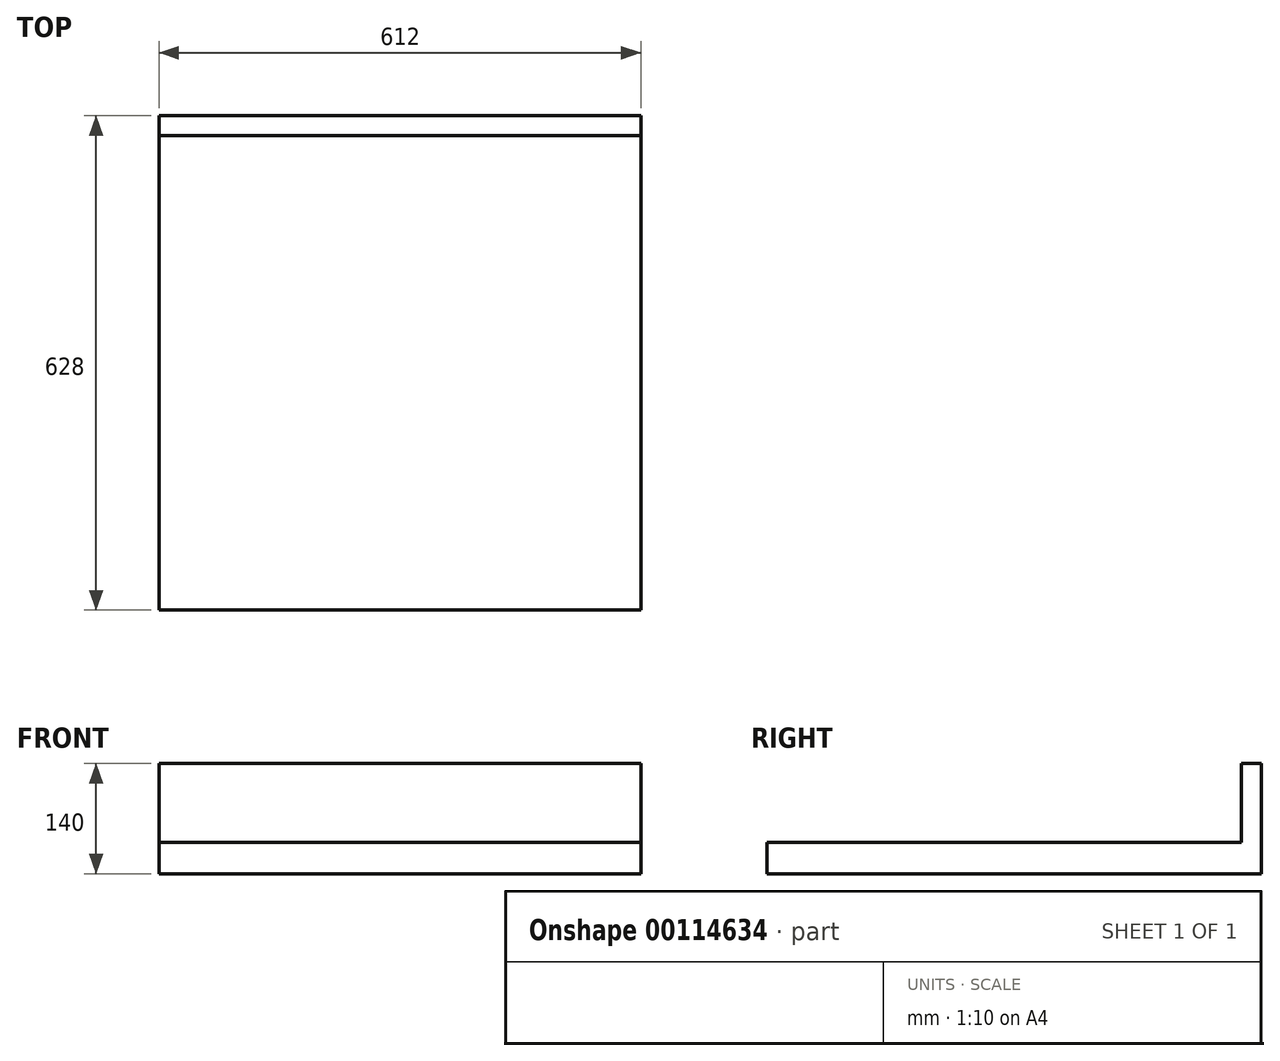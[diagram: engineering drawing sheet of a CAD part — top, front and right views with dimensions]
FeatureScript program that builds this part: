
annotation { "Feature Type Name" : "Feature", "Feature Type Description" : "" }
export const myFeature = defineFeature(function(context is Context, id is Id, definition is map)
    precondition{}
    {
        {
            var Q0;
            Q0=qCreatedBy(makeId("Front.planeOp"),FACE);
            var sketch = newSketch(context, id + "F0", { "sketchPlane" : qUnion([Q0])});
            skLineSegment(sketch, "E0.bottom", {"start": v(306, -20) * mm, "end": v(-306, -20) * mm});
            skLineSegment(sketch, "E0.top", {"start": v(306, 20) * mm, "end": v(-306, 20) * mm});
            skLineSegment(sketch, "E0.left", {"start": v(306, -20) * mm, "end": v(306, 20) * mm});
            skLineSegment(sketch, "E0.right", {"start": v(-306, -20) * mm, "end": v(-306, 20) * mm});
            skPoint(sketch, "E0.middle", {"position": v(0, 0) * mm});
            skSolve(sketch);
        }
        {
            var Q0;
            Q0=makeQuery(id+"F0.imprint","IMPRINT",FACE,{"disambiguationData":[TD([[makeQuery(id+"F0.imprint","IMPRINT",EDGE,{"derivedFrom":sQuery(id+"F0.wireOp",EDGE,"E0.bottom")}),-1.0]])]});
            extrude(context, id + "F1", {"entities" : qUnion([Q0]), "depth" : 628 * mm});
        }
        {
            var Q0;
            Q0=makeQuery(id+"F1.opExtrude","CAP_FACE",FACE,{"disambiguationData":[OSD([sQuery(id+"F0.wireOp",EDGE,"E0.bottom"),sQuery(id+"F0.wireOp",EDGE,"E0.top"),sQuery(id+"F0.wireOp",EDGE,"E0.left"),sQuery(id+"F0.wireOp",EDGE,"E0.right")])],"isStart":true});
            var sketch = newSketch(context, id + "F2", { "sketchPlane" : qUnion([Q0])});
            skLineSegment(sketch, "E1.bottom", {"start": v(-306, 20) * mm, "end": v(306, 20) * mm});
            skLineSegment(sketch, "E1.top", {"start": v(-306, 120) * mm, "end": v(306, 120) * mm});
            skLineSegment(sketch, "E1.left", {"start": v(-306, 20) * mm, "end": v(-306, 120) * mm});
            skLineSegment(sketch, "E1.right", {"start": v(306, 20) * mm, "end": v(306, 120) * mm});
            skSolve(sketch);
        }
        {
            var Q0;
            Q0=makeQuery(id+"F2.imprint","IMPRINT",FACE,{"disambiguationData":[TD([[makeQuery(id+"F2.imprint","IMPRINT",EDGE,{"derivedFrom":sQuery(id+"F2.wireOp",EDGE,"E1.bottom")}),1.0]])]});
            extrude(context, id + "F3", {"entities" : qUnion([Q0]), "operationType" : NewBodyOperationType.ADD, "oppositeDirection" : true, "depth" : 25 * mm});
        }
    });
